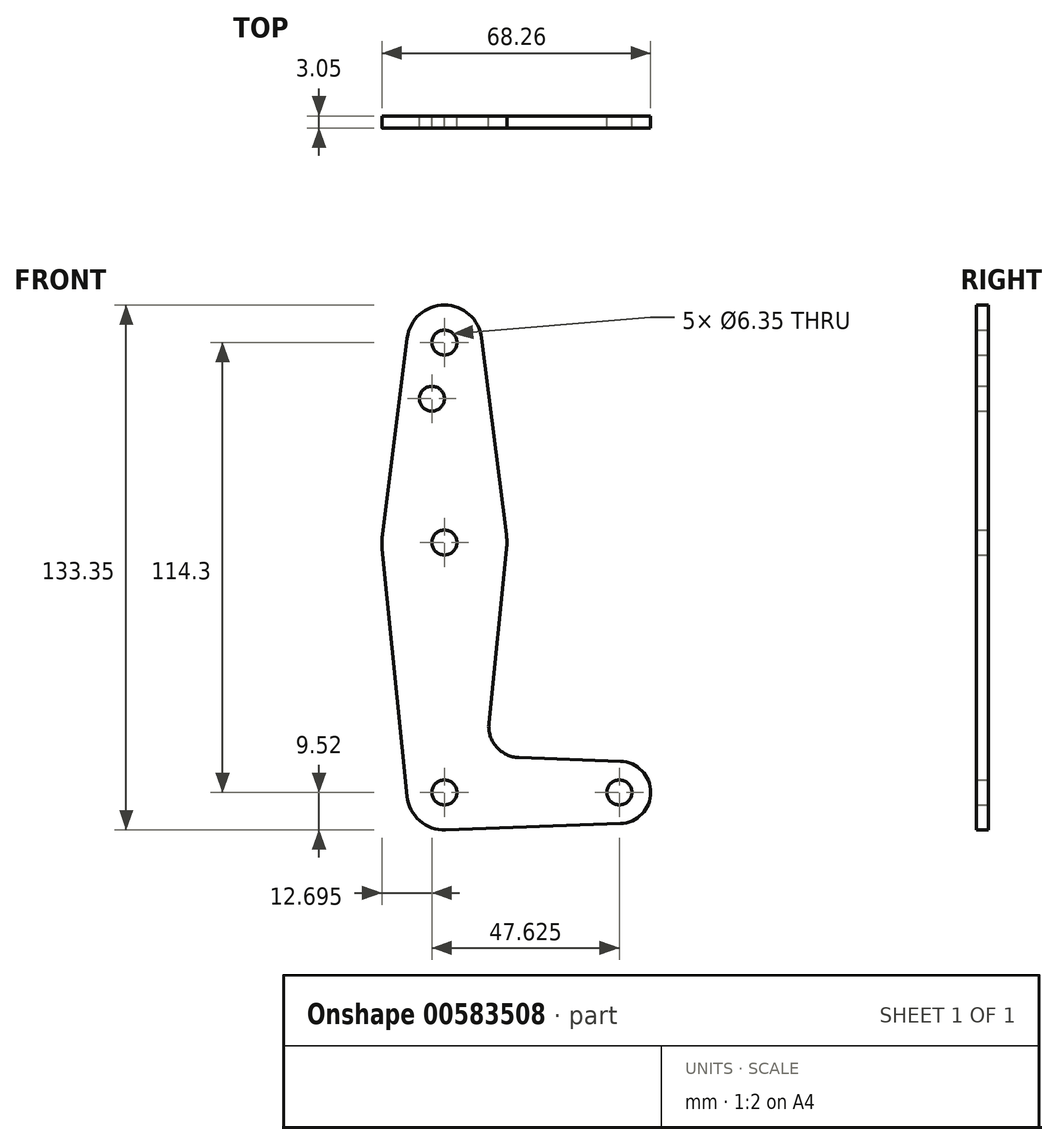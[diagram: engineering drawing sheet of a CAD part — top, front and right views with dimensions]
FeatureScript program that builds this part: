
annotation { "Feature Type Name" : "Feature", "Feature Type Description" : "" }
export const myFeature = defineFeature(function(context is Context, id is Id, definition is map)
    precondition{}
    {
        {
            var Q0;
            Q0=qCreatedBy(makeId("Front.planeOp"),FACE);
            var sketch = newSketch(context, id + "F0", { "sketchPlane" : qUnion([Q0])});
            skLineSegment(sketch, "E0", {"start": v(0, 114.3) * mm, "end": v(0, 0) * mm, "construction": true});
            skLineSegment(sketch, "E1", {"start": v(0, 0) * mm, "end": v(44.45, 0) * mm, "construction": true});
            skCircle(sketch, "E2", {"center": v(0, 114.3) * mm, "radius": 9.53 * mm});
            skCircle(sketch, "E3", {"center": v(0, 63.5) * mm, "radius": 15.88 * mm});
            skCircle(sketch, "E4", {"center": v(0, 0) * mm, "radius": 9.53 * mm});
            skCircle(sketch, "E5", {"center": v(44.45, 0) * mm, "radius": 7.94 * mm});
            skLineSegment(sketch, "E6", {"start": v(-9.45, 115.5) * mm, "end": v(-15.75, 65.48) * mm});
            skLineSegment(sketch, "E7", {"start": v(-15.8, 61.91) * mm, "end": v(-9.48, -0.95) * mm});
            skLineSegment(sketch, "E8", {"start": v(0.34, -9.52) * mm, "end": v(44.73, -7.93) * mm});
            skLineSegment(sketch, "E9", {"start": v(44.73, 7.93) * mm, "end": v(18.93, 8.85) * mm});
            skLineSegment(sketch, "E10", {"start": v(11.3, 17.6) * mm, "end": v(15.8, 61.9) * mm});
            skLineSegment(sketch, "E11", {"start": v(15.75, 65.48) * mm, "end": v(9.45, 115.5) * mm});
            skCircle(sketch, "E12", {"center": v(0, 114.3) * mm, "radius": 3.18 * mm});
            skCircle(sketch, "E13", {"center": v(-3.17, 100.03) * mm, "radius": 3.18 * mm});
            skCircle(sketch, "E14", {"center": v(0, 63.5) * mm, "radius": 3.18 * mm});
            skCircle(sketch, "E15", {"center": v(0, 0) * mm, "radius": 3.18 * mm});
            skCircle(sketch, "E16", {"center": v(44.45, 0) * mm, "radius": 3.18 * mm});
            skArc(sketch, "E17.filletArc", {"start": v(11.3, 17.6) * mm, "mid": v(13.22, 11.57) * mm, "end": v(18.93, 8.85) * mm});
            skSolve(sketch);
        }
        {
            var Q0;
            Q0 = qSketchRegion(id + "F0", true);
            extrude(context, id + "F1", {"entities" : qUnion([Q0]), "depth" : 3.05 * mm, "offsetDistance" : 25.4 * mm});
        }
    });
